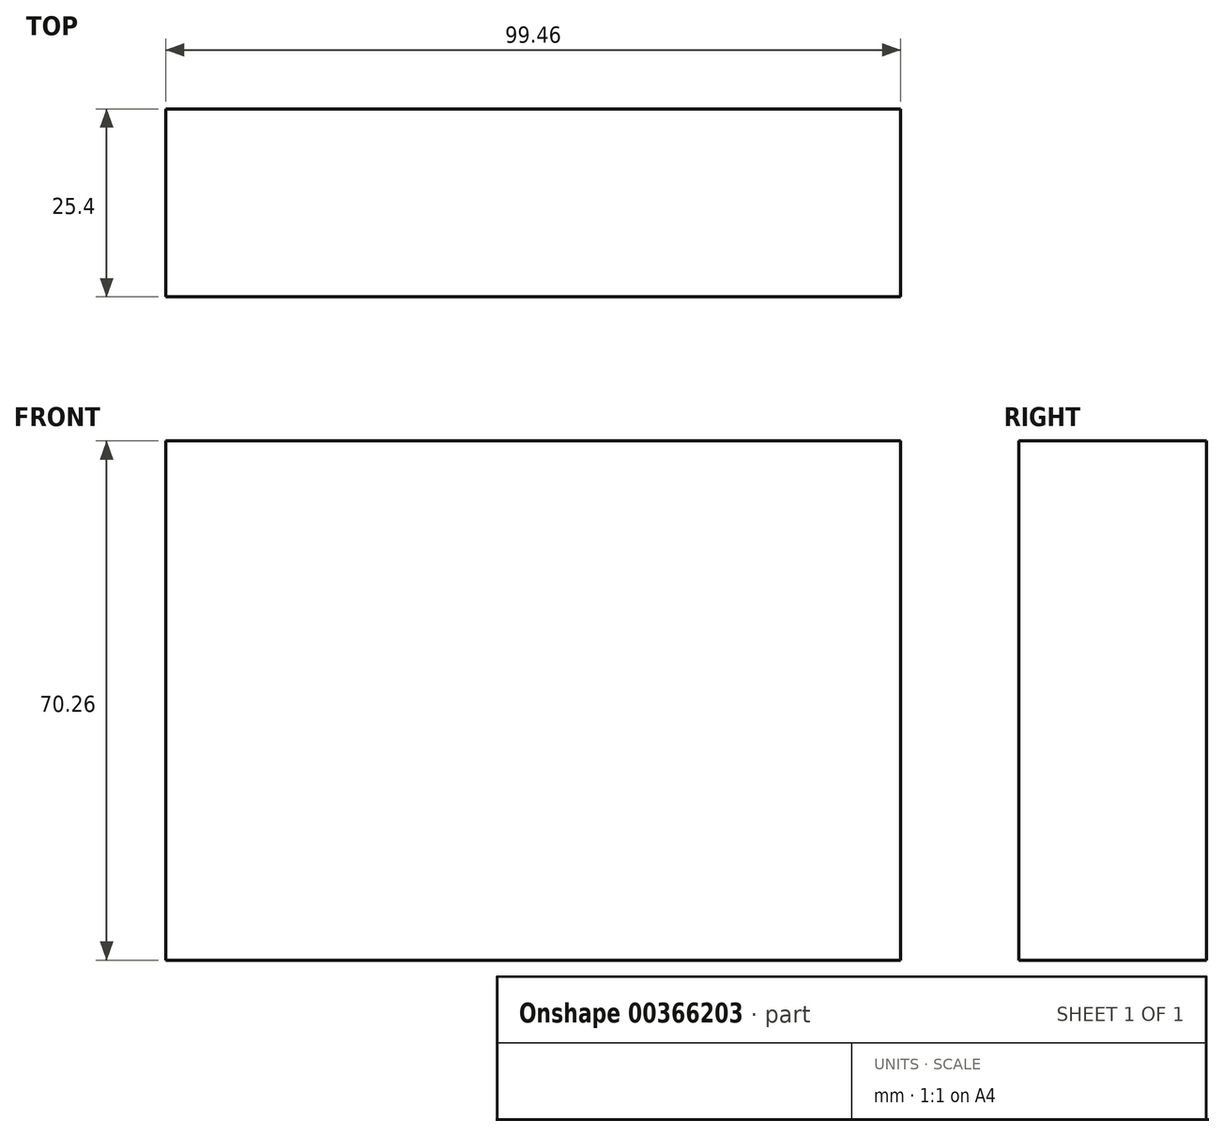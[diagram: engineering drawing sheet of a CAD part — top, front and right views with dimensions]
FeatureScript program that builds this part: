
annotation { "Feature Type Name" : "Feature", "Feature Type Description" : "" }
export const myFeature = defineFeature(function(context is Context, id is Id, definition is map)
    precondition{}
    {
        {
            var Q0;
            Q0=qCreatedBy(makeId("Front.planeOp"),FACE);
            var sketch = newSketch(context, id + "F0", { "sketchPlane" : qUnion([Q0])});
            skLineSegment(sketch, "E0.bottom", {"start": v(0, 0) * mm, "end": v(99.46, 0) * mm});
            skLineSegment(sketch, "E0.top", {"start": v(0, -70.26) * mm, "end": v(99.46, -70.26) * mm});
            skLineSegment(sketch, "E0.left", {"start": v(0, 0) * mm, "end": v(0, -70.26) * mm});
            skLineSegment(sketch, "E0.right", {"start": v(99.46, 0) * mm, "end": v(99.46, -70.26) * mm});
            skSolve(sketch);
        }
        {
            var Q0;
            Q0 = qSketchRegion(id + "F0", true);
            extrude(context, id + "F1", {"entities" : qUnion([Q0]), "depth" : 25.4 * mm});
        }
    });
